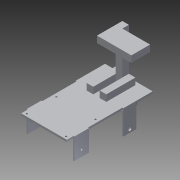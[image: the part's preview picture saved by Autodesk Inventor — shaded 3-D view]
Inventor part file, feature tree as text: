
AUTODESK INVENTOR PART (.ipt)
format: ipt  version: 2014 (Build 180170000, 170)  size: 272,384 bytes
history: native  units: mm
features: sketch x19, extrude x17, plane x4, mirror x3
ambient origin geometry x8: Origin, YZ Plane, XZ Plane, XY Plane, X Axis, Y Axis, Z Axis, Center Point
bodies: Solid1 (feature_tree)
feature tree (43):
  extrude  "Extrusion1"  Depth=20.0mm
  extrude  "Extrusion2"  Depth=20.0mm
  plane  "Work Plane1"
  mirror  "Mirror1"
  extrude  "Extrusion3"  [1 undecoded]
  extrude  "Extrusion10"  Depth=5.0mm
  sketch  "Sketch13"  dims[d26=20.0mm d28=90.0mm d29=20.0mm d31=120.0mm d34=36.0mm d35=0.0mm]
  sketch  "Sketch14"  dims[d36=55.0mm d39=120.0mm]
  plane  "Work Plane2"
  extrude  "Extrusion12"  Depth=20.0mm TaperAngle=0.0deg
  mirror  "Mirror3"
  sketch  "Sketch15"  dims[d44=7.0mm d45=20.0mm]
  extrude  "Extrusion13"  Depth=120.0mm
  mirror  "Mirror4"
  extrude  "Extrusion14"  Depth=20.0mm
  extrude  "Extrusion15"  Depth=75.0mm
  extrude  "Extrusion16"  Depth=10.0mm
  extrude  "Extrusion17"  Depth=3.0mm TaperAngle=0.0deg
  extrude  "Extrusion20"  Depth=10.0mm TaperAngle=0.0deg
  extrude  "Extrusion21"  Depth=50.0mm TaperAngle=0.0deg
  extrude  "Extrusion22"  Depth=50.0mm TaperAngle=0.0deg
  extrude  "Extrusion23"  Depth=20.0mm TaperAngle=0.0deg
  plane  "Work Plane3"
  extrude  "Extrusion24"  Depth=85.0mm TaperAngle=0.0deg
  plane  "Work Plane4"
  extrude  "Extrusion26"  Depth=5.0mm TaperAngle=0.0deg
  extrude  "Extrusion27"  [1 undecoded]
  sketch  "Sketch2"  dims[d0=20.0mm d1=20.0mm]
  sketch  "Sketch3"  dims[d2=210.0mm d3=0.0mm d4=20.0mm]
  sketch  "Sketch4"  dims[d5=100.0mm d6=0.0mm d7=-50.0mm]
  sketch  "Sketch11"  dims[d9=150.0mm d10=0.0mm d25=5.0mm]
  sketch  "Sketch18"  dims[d47=3.0mm d48=0.0mm d51=75.0mm]
  sketch  "Sketch19"  dims[d52=3.0mm d53=0.0mm d54=10.0mm]
  sketch  "Sketch20"  dims[d55=10.0mm d56=3.0mm d57=0.0mm]
  sketch  "Sketch21"  dims[d58=10.0mm d59=0.0mm d60=10.0mm d61=0.0mm]
  sketch  "Sketch22"  dims[d62=3.0mm d63=0.0mm d71=50.0mm d72=0.0mm]
  sketch  "Sketch25"  dims[d73=3.0mm d74=50.0mm d75=0.0mm]
  sketch  "Sketch26"  dims[d76=40.0mm d77=0.0mm d78=20.0mm d79=0.0mm]
  sketch  "Sketch27"  dims[d80=20.0mm d81=0.0mm d87=85.0mm d88=0.0mm]
  sketch  "Sketch28"  dims[d89=3.0mm d90=5.0mm d91=0.0mm]
  sketch  "Sketch29"
  sketch  "Sketch32"
  sketch  "Sketch34"
note: 2 required parameter values undecoded (feature->parameter linkage not recoverable at this tier; creation-order binding heuristic only, values carry confidence <= 0.55)
